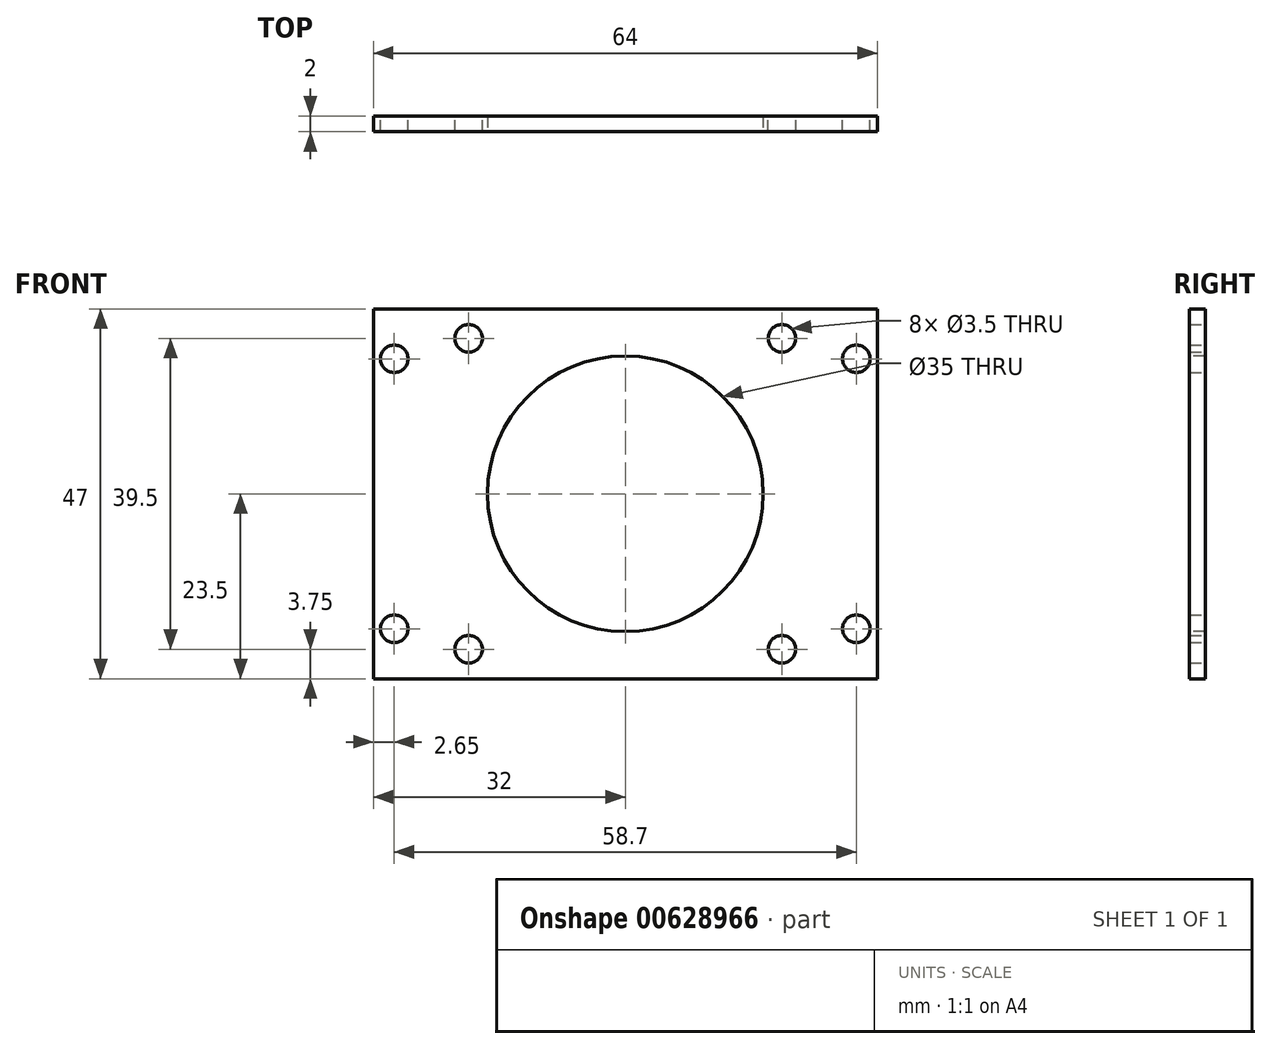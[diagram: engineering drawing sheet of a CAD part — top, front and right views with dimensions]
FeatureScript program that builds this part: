
annotation { "Feature Type Name" : "Feature", "Feature Type Description" : "" }
export const myFeature = defineFeature(function(context is Context, id is Id, definition is map)
    precondition{}
    {
        {
            var Q0;
            Q0=qCreatedBy(makeId("Front.planeOp"),FACE);
            var sketch = newSketch(context, id + "F0", { "sketchPlane" : qUnion([Q0])});
            skLineSegment(sketch, "E0.bottom", {"start": v(32, -23.5) * mm, "end": v(-32, -23.5) * mm});
            skLineSegment(sketch, "E0.top", {"start": v(32, 23.5) * mm, "end": v(-32, 23.5) * mm});
            skLineSegment(sketch, "E0.left", {"start": v(32, -23.5) * mm, "end": v(32, 23.5) * mm});
            skLineSegment(sketch, "E0.right", {"start": v(-32, -23.5) * mm, "end": v(-32, 23.5) * mm});
            skPoint(sketch, "E0.middle", {"position": v(0, 0) * mm});
            skLineSegment(sketch, "E1.bottom", {"start": v(19.9, -19.75) * mm, "end": v(-19.9, -19.75) * mm, "construction": true});
            skLineSegment(sketch, "E1.top", {"start": v(19.9, 19.75) * mm, "end": v(-19.9, 19.75) * mm, "construction": true});
            skLineSegment(sketch, "E1.left", {"start": v(19.9, -19.75) * mm, "end": v(19.9, 19.75) * mm, "construction": true});
            skLineSegment(sketch, "E1.right", {"start": v(-19.9, -19.75) * mm, "end": v(-19.9, 19.75) * mm, "construction": true});
            skLineSegment(sketch, "E2.bottom", {"start": v(29.35, -17.15) * mm, "end": v(-29.35, -17.15) * mm, "construction": true});
            skLineSegment(sketch, "E2.top", {"start": v(29.35, 17.15) * mm, "end": v(-29.35, 17.15) * mm, "construction": true});
            skLineSegment(sketch, "E2.left", {"start": v(29.35, -17.15) * mm, "end": v(29.35, 17.15) * mm, "construction": true});
            skLineSegment(sketch, "E2.right", {"start": v(-29.35, -17.15) * mm, "end": v(-29.35, 17.15) * mm, "construction": true});
            skSolve(sketch);
        }
        {
            var Q0;
            Q0=makeQuery(id+"F0.imprint","IMPRINT",FACE,{"disambiguationData":[TD([[makeQuery(id+"F0.imprint","IMPRINT",EDGE,{"derivedFrom":sQuery(id+"F0.wireOp",EDGE,"E0.bottom")}),-1.0]])]});
            extrude(context, id + "F1", {"entities" : qUnion([Q0]), "depth" : 2 * mm, "offsetDistance" : 25 * mm});
        }
        {
            var Q0;
            Q0=sQuery(id+"F0.wireOp",VERTEX,"E2.right.end");
            var Q1;
            Q1=sQuery(id+"F0.wireOp",VERTEX,"E1.right.end");
            var Q2;
            Q2=sQuery(id+"F0.wireOp",VERTEX,"E1.left.end");
            var Q3;
            Q3=sQuery(id+"F0.wireOp",VERTEX,"E2.top.start");
            var Q4;
            Q4=sQuery(id+"F0.wireOp",VERTEX,"E2.bottom.start");
            var Q5;
            Q5=sQuery(id+"F0.wireOp",VERTEX,"E1.left.start");
            var Q6;
            Q6=sQuery(id+"F0.wireOp",VERTEX,"E1.right.start");
            var Q7;
            Q7=sQuery(id+"F0.wireOp",VERTEX,"E2.bottom.end");
            var Q8;
            Q8=makeQuery(id+"F1.opExtrude","SWEPT_BODY",BODY,{"disambiguationData":[OSD([sQuery(id+"F0.wireOp",EDGE,"E0.bottom"),sQuery(id+"F0.wireOp",EDGE,"E0.top"),sQuery(id+"F0.wireOp",EDGE,"E0.left"),sQuery(id+"F0.wireOp",EDGE,"E0.right")])]});
            hole(context, id + "F2", {"style" : HoleStyle.SIMPLE, "endStyle" : HoleEndStyle.THROUGH, "oppositeDirection" : true, "holeDiameter" : 3.5 * mm, "majorDiameter" : 5 * mm, "isTappedThrough" : true, "tappedDepth" : 2.3 * mm, "tapClearance" : 3, "startFromSketch" : true, "locations" : qUnion([Q0, Q1, Q2, Q3, Q4, Q5, Q6, Q7]), "scope" : qUnion([Q8])});
        }
        {
            var Q0;
            Q0=makeQuery(id+"F1.opExtrude","CAP_FACE",FACE,{"disambiguationData":[OSD([sQuery(id+"F0.wireOp",EDGE,"E0.bottom"),sQuery(id+"F0.wireOp",EDGE,"E0.top"),sQuery(id+"F0.wireOp",EDGE,"E0.left"),sQuery(id+"F0.wireOp",EDGE,"E0.right")])],"isStart":false});
            var sketch = newSketch(context, id + "F3", { "sketchPlane" : qUnion([Q0])});
            skCircle(sketch, "E3", {"center": v(0, 0) * mm, "radius": 17.5 * mm});
            skSolve(sketch);
        }
        {
            var Q0;
            Q0=makeQuery(id+"F3.imprint","IMPRINT",FACE,{"disambiguationData":[TD([[makeQuery(id+"F3.imprint","IMPRINT",EDGE,{"derivedFrom":sQuery(id+"F3.wireOp",EDGE,"E3")}),1.0]])]});
            extrude(context, id + "F4", {"entities" : qUnion([Q0]), "operationType" : NewBodyOperationType.REMOVE, "oppositeDirection" : true, "depth" : 25 * mm, "offsetDistance" : 25 * mm});
        }
    });
